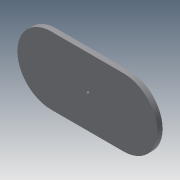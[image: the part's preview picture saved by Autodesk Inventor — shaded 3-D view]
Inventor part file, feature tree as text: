
AUTODESK INVENTOR PART (.ipt)
format: ipt  version: 2013 (Build 170138000, 138)  size: 88,576 bytes
history: native  units: mm
features: extrude x3, sketch x3
ambient origin geometry x8: Origin, YZ Plane, XZ Plane, XY Plane, X Axis, Y Axis, Z Axis, Center Point
bodies: Solid1 (feature_tree)
feature tree (6):
  extrude  "Extrusion1"  Depth=131.0mm
  extrude  "Extrusion2"  Depth=10.0mm TaperAngle=0.0deg
  extrude  "Extrusion3"  Depth=10.0mm TaperAngle=0.0deg
  sketch  "Sketch1"  dims[d0=140.0mm d1=131.0mm]
  sketch  "Sketch2"  dims[d2=15.0mm d3=10.0mm d4=0.0mm]
  sketch  "Sketch3"  dims[d5=6.0mm d6=10.0mm d7=0.0mm d10=100.0mm d11=100.0mm d12=10.0mm d13=0.0mm]
